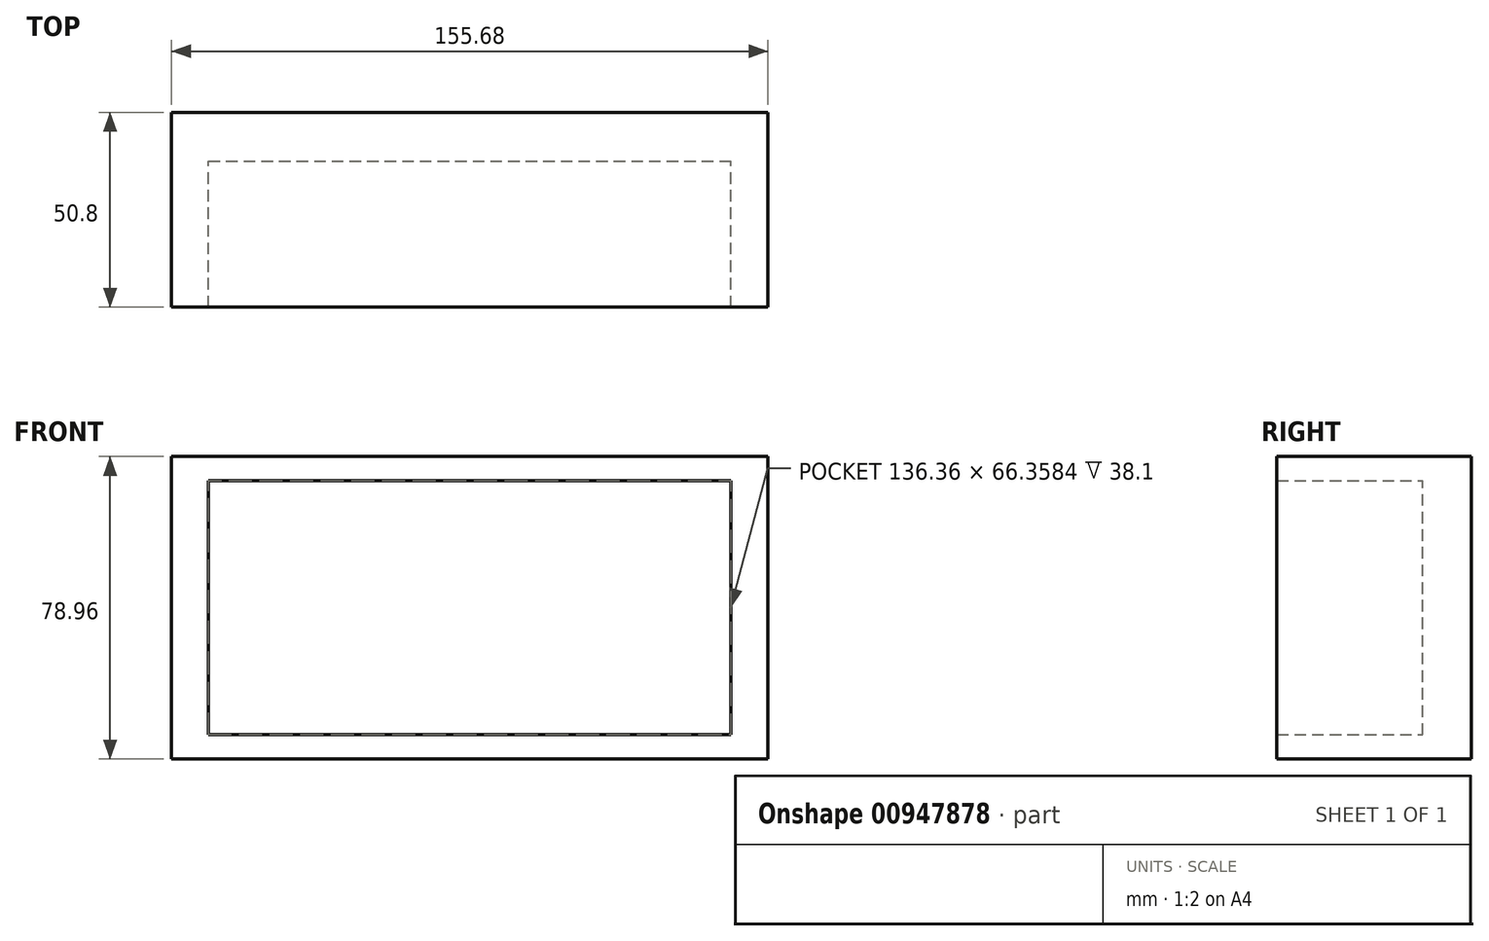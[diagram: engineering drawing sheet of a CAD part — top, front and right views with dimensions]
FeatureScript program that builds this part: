
annotation { "Feature Type Name" : "Feature", "Feature Type Description" : "" }
export const myFeature = defineFeature(function(context is Context, id is Id, definition is map)
    precondition{}
    {
        {
            var Q0;
            Q0=qCreatedBy(makeId("Front.planeOp"),FACE);
            var sketch = newSketch(context, id + "F0", { "sketchPlane" : qUnion([Q0])});
            skLineSegment(sketch, "E0.bottom", {"start": v(0, 0) * mm, "end": v(-68.18, 0) * mm});
            skLineSegment(sketch, "E0.top", {"start": v(0, 33.18) * mm, "end": v(-68.18, 33.18) * mm});
            skLineSegment(sketch, "E0.left", {"start": v(0, 0) * mm, "end": v(0, 33.18) * mm});
            skLineSegment(sketch, "E0.right", {"start": v(-68.18, 0) * mm, "end": v(-68.18, 33.18) * mm});
            skLineSegment(sketch, "E1.MirrorCS", {"start": v(-68.18, 0) * mm, "end": v(-68.18, -33.18) * mm});
            skLineSegment(sketch, "E2.MirrorCS", {"start": v(0, -33.18) * mm, "end": v(-68.18, -33.18) * mm});
            skLineSegment(sketch, "E3.MirrorCS", {"start": v(0, 0) * mm, "end": v(68.18, 0) * mm});
            skLineSegment(sketch, "E4.MirrorCS", {"start": v(68.18, 0) * mm, "end": v(68.18, 33.18) * mm});
            skLineSegment(sketch, "E5.MirrorCS", {"start": v(68.18, 0) * mm, "end": v(68.18, -33.18) * mm});
            skLineSegment(sketch, "E6.MirrorCS", {"start": v(0, -33.18) * mm, "end": v(68.18, -33.18) * mm});
            skLineSegment(sketch, "E7.MirrorCS", {"start": v(0, 33.18) * mm, "end": v(68.18, 33.18) * mm});
            skLineSegment(sketch, "E8.bottom", {"start": v(0, 0) * mm, "end": v(-77.84, 0) * mm});
            skLineSegment(sketch, "E8.top", {"start": v(0, 39.48) * mm, "end": v(-77.84, 39.48) * mm});
            skLineSegment(sketch, "E8.left", {"start": v(0, 0) * mm, "end": v(0, 39.48) * mm});
            skLineSegment(sketch, "E8.right", {"start": v(-77.84, 0) * mm, "end": v(-77.84, 39.48) * mm});
            skLineSegment(sketch, "E9.MirrorCS", {"start": v(0, 39.48) * mm, "end": v(77.84, 39.48) * mm});
            skLineSegment(sketch, "E10.MirrorCS", {"start": v(77.84, 0) * mm, "end": v(77.84, 39.48) * mm});
            skLineSegment(sketch, "E11.MirrorCS", {"start": v(0, 0) * mm, "end": v(77.84, 0) * mm});
            skLineSegment(sketch, "E12.MirrorCS", {"start": v(0, -39.48) * mm, "end": v(-77.84, -39.48) * mm});
            skLineSegment(sketch, "E13.MirrorCS", {"start": v(-77.84, 0) * mm, "end": v(-77.84, -39.48) * mm});
            skLineSegment(sketch, "E14.MirrorCS", {"start": v(77.84, 0) * mm, "end": v(77.84, -39.48) * mm});
            skLineSegment(sketch, "E15.MirrorCS", {"start": v(0, -39.48) * mm, "end": v(77.84, -39.48) * mm});
            skLineSegment(sketch, "E16.MirrorCS", {"start": v(0, 0) * mm, "end": v(0, -39.48) * mm});
            skSolve(sketch);
        }
        {
            var Q0;
            Q0 = qSketchRegion(id + "F0", true);
            extrude(context, id + "F1", {"entities" : qUnion([Q0]), "depth" : 50.8 * mm, "offsetDistance" : 25.4 * mm});
        }
        {
            var Q0;
            {var subQ0=sQuery(id+"F0.wireOp",EDGE,"E0.top");Q0=makeQuery(id+"F0.imprint","IMPRINT",FACE,{"disambiguationData":[TD([[makeQuery(id+"F0.imprint","IMPRINT",EDGE,{"derivedFrom":subQ0}),1.0]])]});}
            var Q1;
            {var subQ0=sQuery(id+"F0.wireOp",EDGE,"E4.MirrorCS");Q1=makeQuery(id+"F0.imprint","IMPRINT",FACE,{"disambiguationData":[TD([[makeQuery(id+"F0.imprint","IMPRINT",EDGE,{"derivedFrom":subQ0}),1.0]])]});}
            var Q2;
            {var subQ0=sQuery(id+"F0.wireOp",EDGE,"E5.MirrorCS");Q2=makeQuery(id+"F0.imprint","IMPRINT",FACE,{"disambiguationData":[TD([[makeQuery(id+"F0.imprint","IMPRINT",EDGE,{"derivedFrom":subQ0}),-1.0]])]});}
            var Q3;
            {var subQ0=sQuery(id+"F0.wireOp",EDGE,"E1.MirrorCS");Q3=makeQuery(id+"F0.imprint","IMPRINT",FACE,{"disambiguationData":[TD([[makeQuery(id+"F0.imprint","IMPRINT",EDGE,{"derivedFrom":subQ0}),1.0]])]});}
            extrude(context, id + "F2", {"entities" : qUnion([Q0, Q1, Q2, Q3]), "operationType" : NewBodyOperationType.ADD, "depth" : 12.7 * mm, "offsetDistance" : 25.4 * mm});
        }
    });
